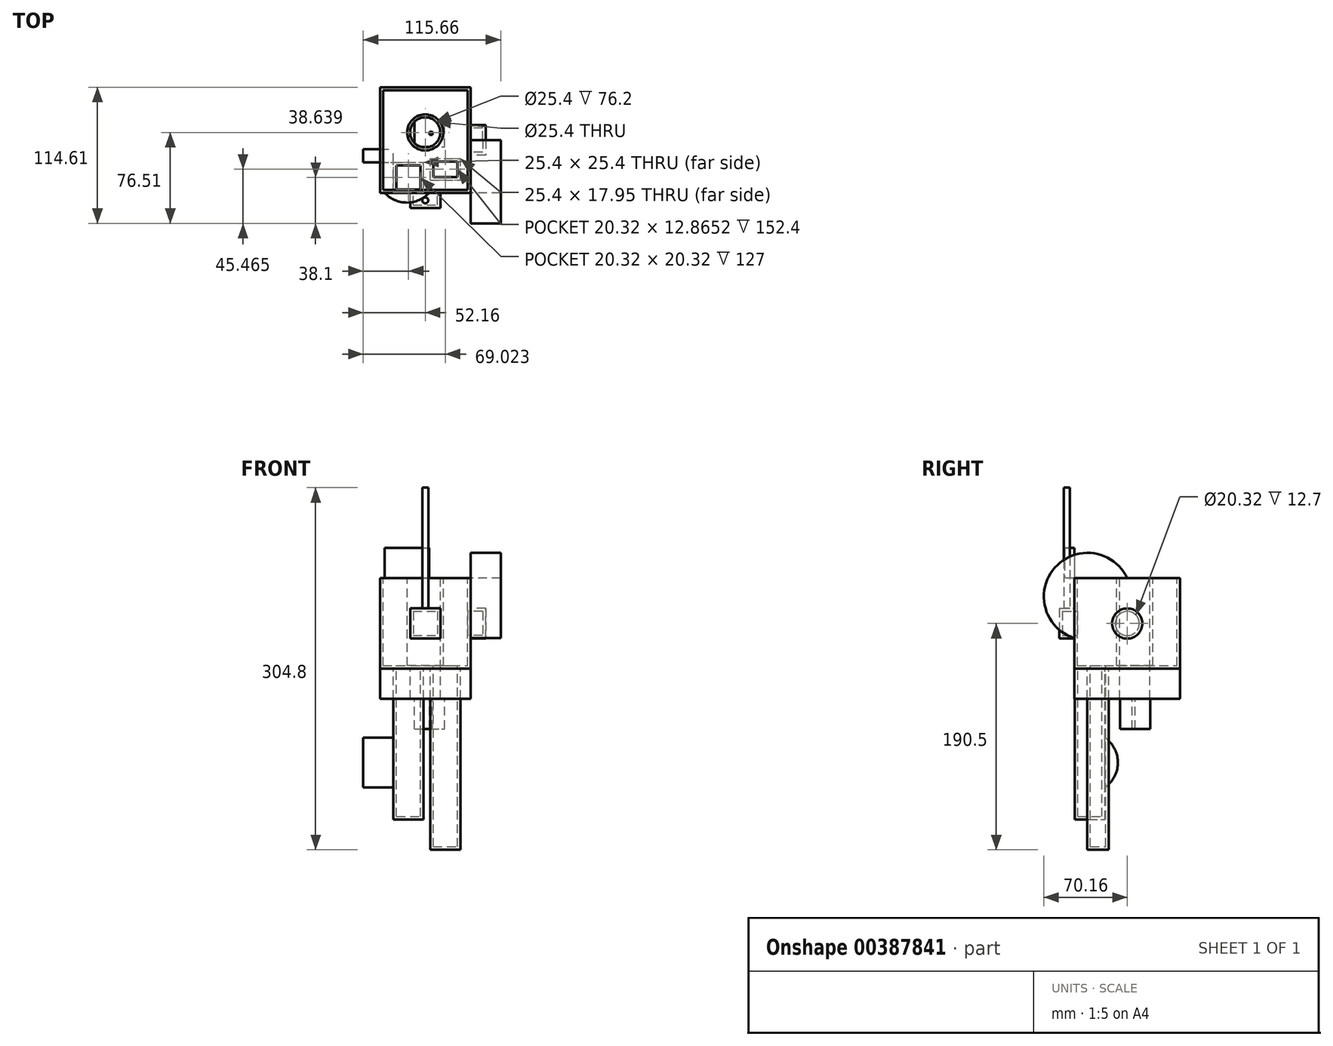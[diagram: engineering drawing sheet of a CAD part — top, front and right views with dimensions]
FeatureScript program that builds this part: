
annotation { "Feature Type Name" : "Feature", "Feature Type Description" : "" }
export const myFeature = defineFeature(function(context is Context, id is Id, definition is map)
    precondition{}
    {
        {
            var Q0;
            Q0=qCreatedBy(makeId("Front.planeOp"),FACE);
            var sketch = newSketch(context, id + "F0", { "sketchPlane" : qUnion([Q0])});
            skLineSegment(sketch, "E0.bottom", {"start": v(0, 0) * mm, "end": v(76.2, 0) * mm});
            skLineSegment(sketch, "E0.top", {"start": v(0, 76.2) * mm, "end": v(76.2, 76.2) * mm});
            skLineSegment(sketch, "E0.left", {"start": v(0, 0) * mm, "end": v(0, 76.2) * mm});
            skLineSegment(sketch, "E0.right", {"start": v(76.2, 0) * mm, "end": v(76.2, 76.2) * mm});
            skSolve(sketch);
        }
        {
            var Q0;
            Q0=makeQuery(id+"F0.imprint","IMPRINT",FACE,{"disambiguationData":[TD([[makeQuery(id+"F0.imprint","IMPRINT",EDGE,{"derivedFrom":sQuery(id+"F0.wireOp",EDGE,"E0.bottom")}),1.0]])]});
            extrude(context, id + "F1", {"entities" : qUnion([Q0]), "depth" : 76.2 * mm});
        }
        {
            var Q0;
            Q0=makeQuery(id+"F1.opExtrude","SWEPT_FACE",FACE,{"disambiguationData":[OSD([sQuery(id+"F0.wireOp",EDGE,"E0.top")])]});
            var sketch = newSketch(context, id + "F2", { "sketchPlane" : qUnion([Q0])});
            skPoint(sketch, "E1", {"position": v(38.1, -38.1) * mm});
            skPoint(sketch, "E1.positionSnap0", {"position": v(38.1, 0) * mm});
            skPoint(sketch, "E1.positionSnap1", {"position": v(0, -38.1) * mm});
            skSolve(sketch);
        }
        {
            var Q0;
            Q0=sQuery(id+"F2.wireOp",VERTEX,"E1");
            var Q1;
            Q1=makeQuery(id+"F1.opExtrude","SWEPT_BODY",BODY,{"disambiguationData":[OSD([sQuery(id+"F0.wireOp",EDGE,"E0.bottom"),sQuery(id+"F0.wireOp",EDGE,"E0.top"),sQuery(id+"F0.wireOp",EDGE,"E0.left"),sQuery(id+"F0.wireOp",EDGE,"E0.right")])]});
            hole(context, id + "F3", {"style" : HoleStyle.SIMPLE, "endStyle" : HoleEndStyle.THROUGH, "holeDiameter" : 25.4 * mm, "isTappedThrough" : true, "tappedDepth" : 12.7 * mm, "tapClearance" : 3, "locations" : qUnion([Q0]), "scope" : qUnion([Q1])});
        }
        {
            var Q0;
            Q0=makeQuery(id+"F1.opExtrude","CAP_FACE",FACE,{"disambiguationData":[OSD([sQuery(id+"F0.wireOp",EDGE,"E0.bottom"),sQuery(id+"F0.wireOp",EDGE,"E0.top"),sQuery(id+"F0.wireOp",EDGE,"E0.left"),sQuery(id+"F0.wireOp",EDGE,"E0.right")])],"isStart":false});
            var sketch = newSketch(context, id + "F4", { "sketchPlane" : qUnion([Q0])});
            skSolve(sketch);
        }
        {
            var Q0;
            Q0=makeQuery(id+"F4.imprint","IMPRINT",FACE,{"disambiguationData":[TD([[makeQuery(id+"F4.imprint","IMPRINT",EDGE,{"derivedFrom":makeQuery(id+"F1.opExtrude","CAP_EDGE",EDGE,{"disambiguationData":[OSD([sQuery(id+"F0.wireOp",EDGE,"E0.bottom")])],"isStart":false})}),1.0]])]});
            var sketch = newSketch(context, id + "F5", { "sketchPlane" : qUnion([Q0])});
            skLineSegment(sketch, "E2.bottom", {"start": v(30.04, 51.25) * mm, "end": v(55.44, 51.25) * mm});
            skLineSegment(sketch, "E2.top", {"start": v(30.04, 25.85) * mm, "end": v(55.44, 25.85) * mm});
            skLineSegment(sketch, "E2.left", {"start": v(30.04, 51.25) * mm, "end": v(30.04, 25.85) * mm});
            skLineSegment(sketch, "E2.right", {"start": v(55.44, 51.25) * mm, "end": v(55.44, 25.85) * mm});
            skSolve(sketch);
        }
        {
            var Q0;
            Q0=makeQuery(id+"F5.imprint","IMPRINT",FACE,{"disambiguationData":[TD([[makeQuery(id+"F5.imprint","IMPRINT",EDGE,{"derivedFrom":sQuery(id+"F5.wireOp",EDGE,"E2.bottom")}),-1.0]])]});
            var Q1;
            Q1=makeQuery(id+"F5.imprint","IMPRINT",FACE,{"disambiguationData":[TD([[makeQuery(id+"F5.imprint","IMPRINT",EDGE,{"derivedFrom":sQuery(id+"F5.wireOp",EDGE,"E2.bottom")}),1.0]])]});
            var Q2;
            Q2=makeQuery(id+"F1.opExtrude","CAP_FACE",FACE,{"disambiguationData":[OSD([sQuery(id+"F0.wireOp",EDGE,"E0.bottom"),sQuery(id+"F0.wireOp",EDGE,"E0.top"),sQuery(id+"F0.wireOp",EDGE,"E0.left"),sQuery(id+"F0.wireOp",EDGE,"E0.right")])],"isStart":false});
            var Q3;
            Q3=makeQuery(id+"F1.opExtrude","CAP_FACE",FACE,{"disambiguationData":[OSD([sQuery(id+"F0.wireOp",EDGE,"E0.bottom"),sQuery(id+"F0.wireOp",EDGE,"E0.top"),sQuery(id+"F0.wireOp",EDGE,"E0.left"),sQuery(id+"F0.wireOp",EDGE,"E0.right")])],"isStart":true});
            var Q4;
            Q4=makeQuery(id+"F4.imprint","IMPRINT",FACE,{"disambiguationData":[TD([[makeQuery(id+"F4.imprint","IMPRINT",EDGE,{"derivedFrom":makeQuery(id+"F1.opExtrude","CAP_EDGE",EDGE,{"disambiguationData":[OSD([sQuery(id+"F0.wireOp",EDGE,"E0.bottom")])],"isStart":false})}),1.0]])]});
            extrude(context, id + "F6", {"entities" : qUnion([Q0, Q1, Q2, Q3, Q4]), "operationType" : NewBodyOperationType.ADD, "depth" : 12.7 * mm});
        }
        {
            var Q0;
            {var subQ0=sQuery(id+"F0.wireOp",EDGE,"E0.right");var subQ1=sQuery(id+"F0.wireOp",EDGE,"E0.left");var subQ2=sQuery(id+"F0.wireOp",EDGE,"E0.top");var subQ3=sQuery(id+"F0.wireOp",EDGE,"E0.bottom");Q0=makeQuery(id+"F6.opExtrude","CAP_FACE",FACE,{"disambiguationData":[OSD([subQ3,subQ2,subQ1,subQ0]),TDD([makeQuery(id+"F1.opExtrude","CAP_FACE",FACE,{"disambiguationData":[OSD([subQ3,subQ2,subQ1,subQ0])],"isStart":false})])],"isStart":false});}
            var sketch = newSketch(context, id + "F7", { "sketchPlane" : qUnion([Q0])});
            skLineSegment(sketch, "E3.bottom", {"start": v(25.4, 50.8) * mm, "end": v(50.8, 50.8) * mm});
            skLineSegment(sketch, "E3.top", {"start": v(25.4, 25.4) * mm, "end": v(50.8, 25.4) * mm});
            skLineSegment(sketch, "E3.left", {"start": v(25.4, 50.8) * mm, "end": v(25.4, 25.4) * mm});
            skLineSegment(sketch, "E3.right", {"start": v(50.8, 50.8) * mm, "end": v(50.8, 25.4) * mm});
            skSolve(sketch);
        }
        {
            var Q0;
            Q0=makeQuery(id+"F7.imprint","IMPRINT",FACE,{"disambiguationData":[TD([[makeQuery(id+"F7.imprint","IMPRINT",EDGE,{"derivedFrom":sQuery(id+"F7.wireOp",EDGE,"E3.bottom")}),-1.0]])]});
            extrude(context, id + "F8", {"entities" : qUnion([Q0]), "operationType" : NewBodyOperationType.ADD, "depth" : 12.7 * mm});
        }
        {
            var Q0;
            {var subQ0=sQuery(id+"F0.wireOp",EDGE,"E0.right");Q0=makeQuery(id+"F6.boolean.opBoolean","MERGE",FACE,{"derivedFrom":[makeQuery(id+"F1.opExtrude","SWEPT_FACE",FACE,{"disambiguationData":[OSD([subQ0])]}),makeQuery(id+"F6.opExtrude","SWEPT_FACE",FACE,{"disambiguationData":[OSD([subQ0]),TDD([makeQuery(id+"F1.opExtrude","CAP_EDGE",EDGE,{"disambiguationData":[OSD([subQ0])],"isStart":false})])]})]});}
            var sketch = newSketch(context, id + "F9", { "sketchPlane" : qUnion([Q0])});
            skCircle(sketch, "E4", {"center": v(-44.45, 38.1) * mm, "radius": 12.7 * mm});
            skPoint(sketch, "E4.centerSnap0", {"position": v(-44.45, 76.2) * mm});
            skPoint(sketch, "E4.centerSnap1", {"position": v(-88.9, 38.1) * mm});
            skSolve(sketch);
        }
        {
            var Q0;
            Q0 = qSketchRegion(id + "F9", true);
            extrude(context, id + "F10", {"entities" : qUnion([Q0]), "operationType" : NewBodyOperationType.ADD, "depth" : 12.7 * mm});
        }
        {
            var Q0;
            Q0 = qSketchRegion(id + "F9", true);
            extrude(context, id + "F11", {"entities" : qUnion([Q0]), "operationType" : NewBodyOperationType.ADD, "depth" : 12.7 * mm});
        }
        {
            var Q0;
            Q0=makeQuery(id+"F10.opExtrude","CAP_FACE",FACE,{"disambiguationData":[OSD([sQuery(id+"F9.wireOp",EDGE,"E4")])],"isStart":false});
            var sketch = newSketch(context, id + "F12", { "sketchPlane" : qUnion([Q0])});
            skCircle(sketch, "E5", {"center": v(-44.45, 38.1) * mm, "radius": 6.35 * mm});
            skSolve(sketch);
        }
        {
            var Q0;
            {var subQ0=sQuery(id+"F0.wireOp",EDGE,"E0.top");Q0=makeQuery(id+"F6.boolean.opBoolean","MERGE",FACE,{"derivedFrom":[makeQuery(id+"F1.opExtrude","SWEPT_FACE",FACE,{"disambiguationData":[OSD([subQ0])]}),makeQuery(id+"F6.opExtrude","SWEPT_FACE",FACE,{"disambiguationData":[OSD([subQ0]),TDD([makeQuery(id+"F1.opExtrude","CAP_EDGE",EDGE,{"disambiguationData":[OSD([subQ0])],"isStart":false})])]})]});}
            var sketch = newSketch(context, id + "F13", { "sketchPlane" : qUnion([Q0])});
            skArc(sketch, "E6", {"start": v(8.36, -50.77) * mm, "mid": v(12.97, -95.22) * mm, "end": v(47.64, -67.03) * mm});
            skSolve(sketch);
        }
        {
            var Q0;
            {var subQ0=sQuery(id+"F13.wireOp",EDGE,"E6");var subQ1=sQuery(id+"F0.wireOp",EDGE,"E0.top");var subQ2=makeQuery(id+"F6.opExtrude","CAP_EDGE",EDGE,{"disambiguationData":[OSD([subQ1]),TDD([makeQuery(id+"F1.opExtrude","CAP_EDGE",EDGE,{"disambiguationData":[OSD([subQ1])],"isStart":false})])],"isStart":false});var subQ3=makeQuery(id+"F13.imprint","INTERSECT",VERTEX,{"disambiguationData":[OD(0.0)],"derivedFrom":[subQ2,subQ0]});Q0=makeQuery(id+"F13.imprint","IMPRINT",FACE,{"disambiguationData":[TD([[makeQuery(id+"F13.imprint","IMPRINT",EDGE,{"disambiguationData":[TD([[subQ3,1.0]])],"derivedFrom":subQ0}),1.0]])]});}
            extrude(context, id + "F14", {"entities" : qUnion([Q0]), "depth" : 25.4 * mm});
        }
        {
            var Q0;
            {var subQ0=sQuery(id+"F0.wireOp",EDGE,"E0.right");Q0=makeQuery(id+"F6.boolean.opBoolean","MERGE",FACE,{"derivedFrom":[makeQuery(id+"F1.opExtrude","SWEPT_FACE",FACE,{"disambiguationData":[OSD([subQ0])]}),makeQuery(id+"F6.opExtrude","SWEPT_FACE",FACE,{"disambiguationData":[OSD([subQ0]),TDD([makeQuery(id+"F1.opExtrude","CAP_EDGE",EDGE,{"disambiguationData":[OSD([subQ0])],"isStart":false})])]})]});}
            var sketch = newSketch(context, id + "F15", { "sketchPlane" : qUnion([Q0])});
            skArc(sketch, "E7", {"start": v(-44.45, 76.2) * mm, "mid": v(-114.61, 60.6) * mm, "end": v(-44.3, 45.68) * mm});
            skSolve(sketch);
        }
        {
            var Q0;
            {var subQ0=sQuery(id+"F15.wireOp",EDGE,"E7");var subQ1=sQuery(id+"F0.wireOp",EDGE,"E0.right");var subQ5=makeQuery(id+"F6.opExtrude","CAP_EDGE",EDGE,{"disambiguationData":[OSD([subQ1]),TDD([makeQuery(id+"F1.opExtrude","CAP_EDGE",EDGE,{"disambiguationData":[OSD([subQ1])],"isStart":false})])],"isStart":false});var subQ6=makeQuery(id+"F15.imprint","INTERSECT",VERTEX,{"derivedFrom":[subQ5,subQ0]});Q0=makeQuery(id+"F15.imprint","IMPRINT",FACE,{"disambiguationData":[TD([[makeQuery(id+"F15.imprint","IMPRINT",EDGE,{"disambiguationData":[TD([[subQ6,1.0]])],"derivedFrom":subQ0}),1.0]])]});}
            extrude(context, id + "F16", {"entities" : qUnion([Q0]), "depth" : 25.4 * mm});
        }
        {
            var Q0;
            Q0=makeQuery(id+"F8.opExtrude","SWEPT_FACE",FACE,{"disambiguationData":[OSD([sQuery(id+"F7.wireOp",EDGE,"E3.bottom")])]});
            var sketch = newSketch(context, id + "F17", { "sketchPlane" : qUnion([Q0])});
            skCircle(sketch, "E8", {"center": v(38.1, -95.25) * mm, "radius": 2.54 * mm});
            skPoint(sketch, "E8.centerSnap0", {"position": v(38.1, -101.6) * mm});
            skPoint(sketch, "E8.centerSnap1", {"position": v(50.8, -95.25) * mm});
            skSolve(sketch);
        }
        {
            var Q0;
            Q0 = qSketchRegion(id + "F17", true);
            extrude(context, id + "F18", {"entities" : qUnion([Q0]), "operationType" : NewBodyOperationType.ADD, "depth" : 101.6 * mm});
        }
        {
            var Q0;
            Q0=makeQuery(id+"F1.opExtrude","CAP_FACE",FACE,{"disambiguationData":[OSD([sQuery(id+"F0.wireOp",EDGE,"E0.bottom"),sQuery(id+"F0.wireOp",EDGE,"E0.top"),sQuery(id+"F0.wireOp",EDGE,"E0.left"),sQuery(id+"F0.wireOp",EDGE,"E0.right")])],"isStart":true});
            var sketch = newSketch(context, id + "F19", { "sketchPlane" : qUnion([Q0])});
            skArc(sketch, "E9", {"start": v(-57.38, 62.56) * mm, "mid": v(-41.8, 27.4) * mm, "end": v(-26.23, 62.56) * mm});
            skSolve(sketch);
        }
        {
            var Q0;
            Q0=sQuery(id+"F19.wireOp",EDGE,"E9");
            extrude(context, id + "F20", {"bodyType" : ToolBodyType.SURFACE, "surfaceEntities" : qUnion([Q0]), "depth" : 76.2 * mm});
        }
        {
            var Q0;
            Q0=makeQuery(id+"F8.opExtrude","SWEPT_FACE",FACE,{"disambiguationData":[OSD([sQuery(id+"F7.wireOp",EDGE,"E3.top")])]});
            var sketch = newSketch(context, id + "F21", { "sketchPlane" : qUnion([Q0])});
            skLineSegment(sketch, "E10.bottom", {"start": v(42.26, 78.12) * mm, "end": v(67.66, 78.12) * mm});
            skLineSegment(sketch, "E10.top", {"start": v(42.26, 60.17) * mm, "end": v(67.66, 60.17) * mm});
            skLineSegment(sketch, "E10.left", {"start": v(42.26, 78.12) * mm, "end": v(42.26, 60.17) * mm});
            skLineSegment(sketch, "E10.right", {"start": v(67.66, 78.12) * mm, "end": v(67.66, 60.17) * mm});
            skSolve(sketch);
        }
        {
            var Q0;
            Q0 = qSketchRegion(id + "F21", true);
            extrude(context, id + "F22", {"entities" : qUnion([Q0]), "operationType" : NewBodyOperationType.ADD, "depth" : 177.8 * mm});
        }
        {
            var Q0;
            {var subQ0=sQuery(id+"F0.wireOp",EDGE,"E0.bottom");Q0=makeQuery(id+"F6.boolean.opBoolean","MERGE",FACE,{"derivedFrom":[makeQuery(id+"F1.opExtrude","SWEPT_FACE",FACE,{"disambiguationData":[OSD([subQ0])]}),makeQuery(id+"F6.opExtrude","SWEPT_FACE",FACE,{"disambiguationData":[OSD([subQ0]),TDD([makeQuery(id+"F1.opExtrude","CAP_EDGE",EDGE,{"disambiguationData":[OSD([subQ0])],"isStart":false})])]})]});}
            var sketch = newSketch(context, id + "F23", { "sketchPlane" : qUnion([Q0])});
            skLineSegment(sketch, "E11.bottom", {"start": v(11.34, 88.67) * mm, "end": v(36.74, 88.67) * mm});
            skLineSegment(sketch, "E11.top", {"start": v(11.34, 63.27) * mm, "end": v(36.74, 63.27) * mm});
            skLineSegment(sketch, "E11.left", {"start": v(11.34, 88.67) * mm, "end": v(11.34, 63.27) * mm});
            skLineSegment(sketch, "E11.right", {"start": v(36.74, 88.67) * mm, "end": v(36.74, 63.27) * mm});
            skSolve(sketch);
        }
        {
            var Q0;
            Q0 = qSketchRegion(id + "F23", true);
            var Q1;
            Q1=makeQuery(id+"F23.imprint","IMPRINT",FACE,{"disambiguationData":[TD([[makeQuery(id+"F23.imprint","IMPRINT",EDGE,{"derivedFrom":makeQuery(id+"F3.hole-0.boolean.opBoolean","INTERSECT",EDGE,{"derivedFrom":[makeQuery(id+"F1.opExtrude","SWEPT_FACE",FACE,{"disambiguationData":[OSD([sQuery(id+"F0.wireOp",EDGE,"E0.bottom")])]}),makeQuery(id+"F3.hole-0.opRevolve","SWEPT_FACE",FACE,{"disambiguationData":[OSD([sQuery(id+"F3.hole-0.sketch.wireOp",EDGE,"core_line_2")])]})]})}),1.0]])]});
            extrude(context, id + "F24", {"entities" : qUnion([Q0, Q1]), "operationType" : NewBodyOperationType.ADD, "depth" : 127 * mm});
        }
        {
            var Q0;
            {var subQ0=sQuery(id+"F0.wireOp",EDGE,"E0.bottom");Q0=makeQuery(id+"F6.boolean.opBoolean","MERGE",FACE,{"derivedFrom":[makeQuery(id+"F1.opExtrude","SWEPT_FACE",FACE,{"disambiguationData":[OSD([subQ0])]}),makeQuery(id+"F6.opExtrude","SWEPT_FACE",FACE,{"disambiguationData":[OSD([subQ0]),TDD([makeQuery(id+"F1.opExtrude","CAP_EDGE",EDGE,{"disambiguationData":[OSD([subQ0])],"isStart":false})])]})]});}
            extrude(context, id + "F25", {"entities" : qUnion([Q0]), "depth" : 25.4 * mm});
        }
        {
            var Q0;
            Q0=makeQuery(id+"F25.opExtrude","CAP_FACE",FACE,{"disambiguationData":[OSD([sQuery(id+"F0.wireOp",EDGE,"E0.bottom")])],"isStart":false});
            var sketch = newSketch(context, id + "F26", { "sketchPlane" : qUnion([Q0])});
            skLineSegment(sketch, "E12.bottom", {"start": v(28.92, 50.41) * mm, "end": v(54.32, 50.41) * mm});
            skLineSegment(sketch, "E12.top", {"start": v(28.92, 25.01) * mm, "end": v(54.32, 25.01) * mm});
            skLineSegment(sketch, "E12.left", {"start": v(28.92, 50.41) * mm, "end": v(28.92, 25.01) * mm});
            skLineSegment(sketch, "E12.right", {"start": v(54.32, 50.41) * mm, "end": v(54.32, 25.01) * mm});
            skPoint(sketch, "E13.firstSnap0", {"position": v(41.62, 50.41) * mm});
            skPoint(sketch, "E13.firstSnap1", {"position": v(54.32, 37.71) * mm});
            skLineSegment(sketch, "E13.bottom", {"start": v(41.62, 37.71) * mm, "end": v(44.16, 37.71) * mm});
            skLineSegment(sketch, "E13.top", {"start": v(41.62, 40.25) * mm, "end": v(44.16, 40.25) * mm});
            skLineSegment(sketch, "E13.left", {"start": v(41.62, 37.71) * mm, "end": v(41.62, 40.25) * mm});
            skLineSegment(sketch, "E13.right", {"start": v(44.16, 37.71) * mm, "end": v(44.16, 40.25) * mm});
            skSolve(sketch);
        }
        {
            var Q0;
            Q0 = qSketchRegion(id + "F26", true);
            extrude(context, id + "F27", {"entities" : qUnion([Q0]), "depth" : 25.4 * mm});
        }
        {
            var Q0;
            {var subQ0=sQuery(id+"F0.wireOp",EDGE,"E0.top");Q0=makeQuery(id+"F6.boolean.opBoolean","MERGE",FACE,{"derivedFrom":[makeQuery(id+"F1.opExtrude","SWEPT_FACE",FACE,{"disambiguationData":[OSD([subQ0])]}),makeQuery(id+"F6.opExtrude","SWEPT_FACE",FACE,{"disambiguationData":[OSD([subQ0]),TDD([makeQuery(id+"F1.opExtrude","CAP_EDGE",EDGE,{"disambiguationData":[OSD([subQ0])],"isStart":false})])]})]});}
            shell(context, id + "F28", {"entities" : qUnion([Q0]), "thickness" : 2.54 * mm});
        }
        {
            var Q0;
            Q0=makeQuery(id+"F24.opExtrude","SWEPT_FACE",FACE,{"disambiguationData":[OSD([sQuery(id+"F23.wireOp",EDGE,"E11.left")])]});
            var sketch = newSketch(context, id + "F29", { "sketchPlane" : qUnion([Q0])});
            skArc(sketch, "E14", {"start": v(63.27, -58.02) * mm, "mid": v(69.52, -102.95) * mm, "end": v(101.92, -71.2) * mm});
            skSolve(sketch);
        }
        {
            var Q0;
            Q0 = qSketchRegion(id + "F29", true);
            var Q1;
            {var subQ0=sQuery(id+"F29.wireOp",EDGE,"E14");var subQ1=makeQuery(id+"F24.opExtrude","SWEPT_EDGE",EDGE,{"disambiguationData":[OSD([sQuery(id+"F23.wireOp",EDGE,"E11.top"),sQuery(id+"F23.wireOp",EDGE,"E11.left")])]});var subQ2=makeQuery(id+"F29.imprint","INTERSECT",VERTEX,{"disambiguationData":[OD(0.0)],"derivedFrom":[subQ1,subQ0]});Q1=makeQuery(id+"F29.imprint","IMPRINT",FACE,{"disambiguationData":[TD([[makeQuery(id+"F29.imprint","IMPRINT",EDGE,{"disambiguationData":[TD([[subQ2,-1.0]])],"derivedFrom":subQ0}),1.0]])]});}
            extrude(context, id + "F30", {"entities" : qUnion([Q0, Q1]), "depth" : 25.4 * mm});
        }
    });
